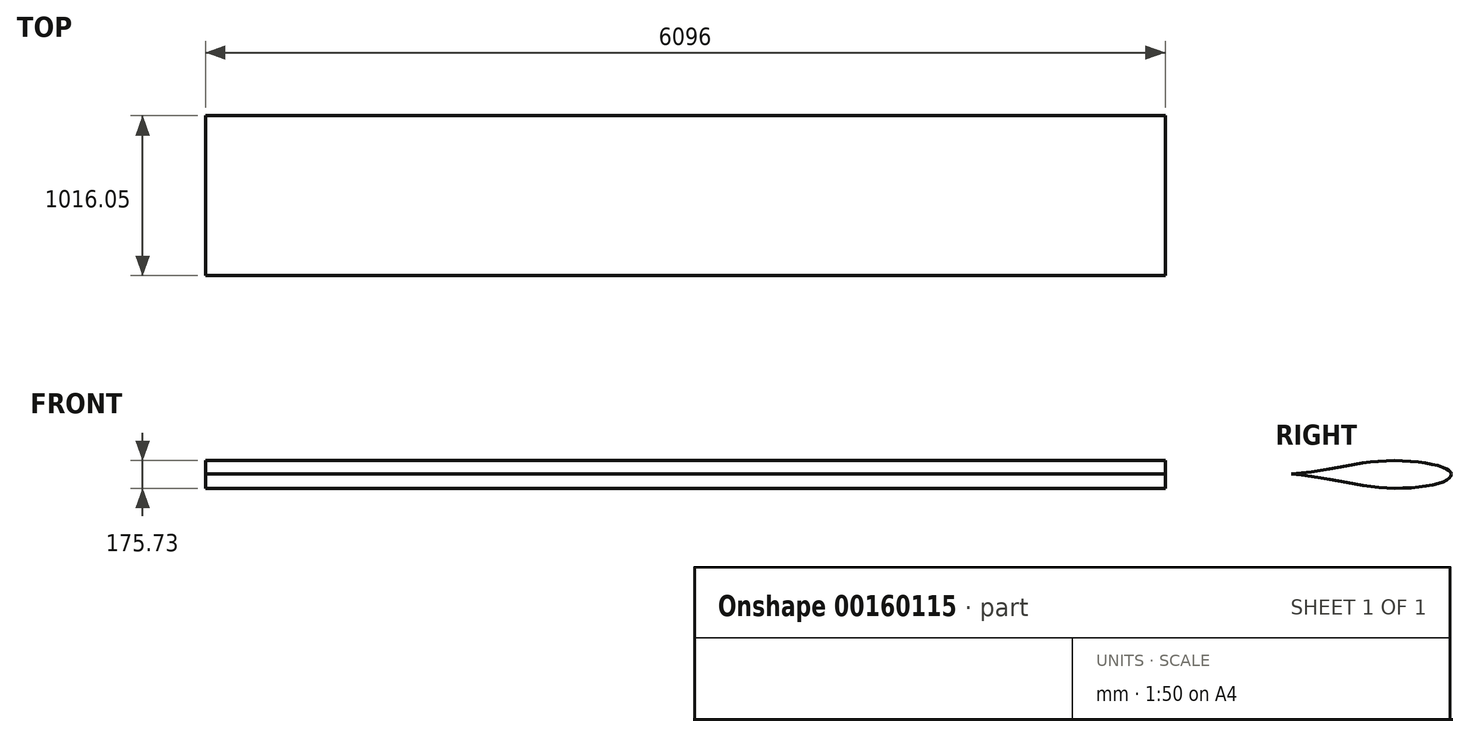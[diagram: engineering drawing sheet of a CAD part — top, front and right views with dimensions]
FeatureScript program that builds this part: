
annotation { "Feature Type Name" : "Feature", "Feature Type Description" : "" }
export const myFeature = defineFeature(function(context is Context, id is Id, definition is map)
    precondition{}
    {
        {
            var Q0;
            Q0=qCreatedBy(makeId("Right.planeOp"),FACE);
            var sketch = newSketch(context, id + "F0", { "sketchPlane" : qUnion([Q0])});
            skFitSpline(sketch, "E0", {"points": [v(0, 0) * mm, v(615.97, -88.32) * mm, v(986.61, -39.76) * mm, v(1016, 0) * mm, v(983.89, 34.68) * mm, v(615.1, 85.36) * mm, v(0, 0.24) * mm], "startDerivative": vector(3107.38, -257.3) * mm, "endDerivative": vector(-3096.3, -281.82) * mm});
            skLineSegment(sketch, "E1", {"start": v(0, 0.24) * mm, "end": v(0, 0) * mm});
            skLineSegment(sketch, "E2", {"start": v(0, 0) * mm, "end": v(1016, 0) * mm});
            skSolve(sketch);
        }
        {
            var Q0;
            {var subQ0=sQuery(id+"F0.wireOp",EDGE,"E2");Q0=makeQuery(id+"F0.imprint","IMPRINT",FACE,{"disambiguationData":[TD([[makeQuery(id+"F0.imprint","IMPRINT",EDGE,{"derivedFrom":subQ0}),-1.0]])]});}
            var Q1;
            {var subQ0=sQuery(id+"F0.wireOp",EDGE,"E1");Q1=makeQuery(id+"F0.imprint","IMPRINT",FACE,{"disambiguationData":[TD([[makeQuery(id+"F0.imprint","IMPRINT",EDGE,{"derivedFrom":subQ0}),1.0]])]});}
            extrude(context, id + "F1", {"entities" : qUnion([Q0, Q1]), "depth" : 6096 * mm});
        }
    });
